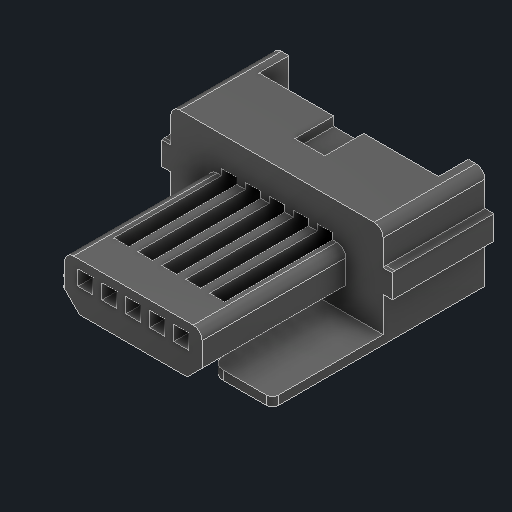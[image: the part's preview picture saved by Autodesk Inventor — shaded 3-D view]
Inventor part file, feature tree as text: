
AUTODESK INVENTOR PART (.ipt)
format: ipt  version: 2023 (Build 270158000, 158)  size: 214,528 bytes
history: native  units: in
note: dims shown in document units (in); Inventor stores cm internally (conversion verified against a paired STEP export)
features: fillet x1
ambient origin geometry x8: Origin, YZ Plane, XZ Plane, XY Plane, X Axis, Y Axis, Z Axis, Center Point
bodies: Solid1 (feature_tree)
feature tree (1):
  fillet  "Fillet3"  [1 undecoded]
note: 1 required parameter value undecoded (feature->parameter linkage not recoverable at this tier; creation-order binding heuristic only, values carry confidence <= 0.55)
